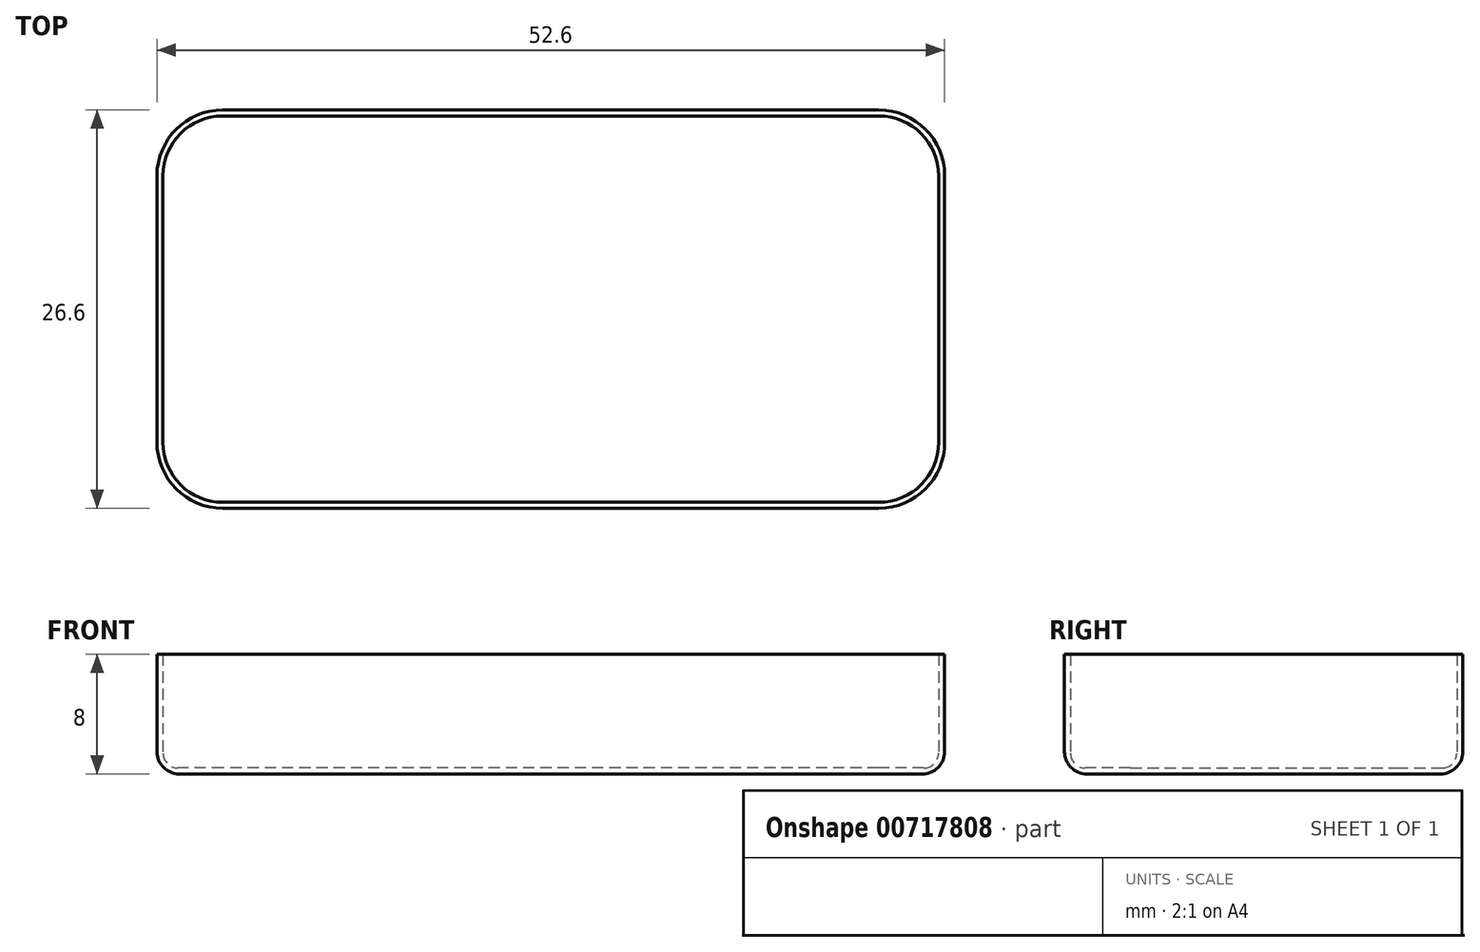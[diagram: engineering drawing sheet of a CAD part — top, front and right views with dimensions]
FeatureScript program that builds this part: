
annotation { "Feature Type Name" : "Feature", "Feature Type Description" : "" }
export const myFeature = defineFeature(function(context is Context, id is Id, definition is map)
    precondition{}
    {
        {
            var Q0;
            Q0=qCreatedBy(makeId("Top.planeOp"),FACE);
            var sketch = newSketch(context, id + "F0", { "sketchPlane" : qUnion([Q0])});
            skLineSegment(sketch, "E0.bottom", {"start": v(26.3, -13.3) * mm, "end": v(-26.3, -13.3) * mm});
            skLineSegment(sketch, "E0.top", {"start": v(26.3, 13.3) * mm, "end": v(-26.3, 13.3) * mm});
            skLineSegment(sketch, "E0.left", {"start": v(26.3, -13.3) * mm, "end": v(26.3, 13.3) * mm});
            skLineSegment(sketch, "E0.right", {"start": v(-26.3, -13.3) * mm, "end": v(-26.3, 13.3) * mm});
            skPoint(sketch, "E0.middle", {"position": v(0, 0) * mm});
            skLineSegment(sketch, "E1.bottom", {"start": v(-25.9, 12.9) * mm, "end": v(25.9, 12.9) * mm});
            skLineSegment(sketch, "E1.top", {"start": v(-25.9, -12.9) * mm, "end": v(25.9, -12.9) * mm});
            skLineSegment(sketch, "E1.left", {"start": v(-25.9, 12.9) * mm, "end": v(-25.9, -12.9) * mm});
            skLineSegment(sketch, "E1.right", {"start": v(25.9, 12.9) * mm, "end": v(25.9, -12.9) * mm});
            skSolve(sketch);
        }
        {
            var Q0;
            Q0=qSketchRegion(id+"F0",true);
            var Q1;
            Q1=makeQuery(id+"F0.imprint","IMPRINT",FACE,{"disambiguationData":[TD([[makeQuery(id+"F0.imprint","IMPRINT",EDGE,{"derivedFrom":sQuery(id+"F0.wireOp",EDGE,"E1.bottom")}),-1.0]])]});
            extrude(context, id + "F1", {"entities" : qUnion([Q0, Q1]), "depth" : .4 * mm, "offsetDistance" : 25 * mm});
        }
        {
            var Q0;
            Q0=makeQuery(id+"F0.imprint","IMPRINT",FACE,{"disambiguationData":[TD([[makeQuery(id+"F0.imprint","IMPRINT",EDGE,{"derivedFrom":sQuery(id+"F0.wireOp",EDGE,"E0.bottom")}),-1.0]])]});
            extrude(context, id + "F2", {"entities" : qUnion([Q0]), "operationType" : NewBodyOperationType.ADD, "depth" : 8 * mm, "offsetDistance" : 25 * mm});
        }
        {
            var Q0;
            Q0=makeQuery(id+"F2.opExtrude","SWEPT_EDGE",EDGE,{"disambiguationData":[OSD([sQuery(id+"F0.wireOp",EDGE,"E1.bottom"),sQuery(id+"F0.wireOp",EDGE,"E1.left")])]});
            var Q1;
            Q1=makeQuery(id+"F2.opExtrude","SWEPT_EDGE",EDGE,{"disambiguationData":[OSD([sQuery(id+"F0.wireOp",EDGE,"E1.bottom"),sQuery(id+"F0.wireOp",EDGE,"E1.right")])]});
            var Q2;
            Q2=makeQuery(id+"F2.opExtrude","SWEPT_EDGE",EDGE,{"disambiguationData":[OSD([sQuery(id+"F0.wireOp",EDGE,"E1.top"),sQuery(id+"F0.wireOp",EDGE,"E1.right")])]});
            var Q3;
            Q3=makeQuery(id+"F2.opExtrude","SWEPT_EDGE",EDGE,{"disambiguationData":[OSD([sQuery(id+"F0.wireOp",EDGE,"E1.top"),sQuery(id+"F0.wireOp",EDGE,"E1.left")])]});
            fillet(context, id + "F3", {"entities" : qUnion([Q0, Q1, Q2, Q3]), "radius" : 4 * mm, "tangentPropagation" : true, "allowEdgeOverflow" : false});
        }
        {
            var Q0;
            {var subQ0=sQuery(id+"F0.wireOp",EDGE,"E0.left");var subQ1=sQuery(id+"F0.wireOp",EDGE,"E0.top");Q0=makeQuery(id+"F2.boolean.opBoolean","MERGE",EDGE,{"derivedFrom":[makeQuery(id+"F1.opExtrude","SWEPT_EDGE",EDGE,{"disambiguationData":[OSD([subQ1,subQ0])]}),makeQuery(id+"F2.opExtrude","SWEPT_EDGE",EDGE,{"disambiguationData":[OSD([subQ1,subQ0])]})]});}
            var Q1;
            {var subQ0=sQuery(id+"F0.wireOp",EDGE,"E0.left");var subQ1=sQuery(id+"F0.wireOp",EDGE,"E0.bottom");Q1=makeQuery(id+"F2.boolean.opBoolean","MERGE",EDGE,{"derivedFrom":[makeQuery(id+"F1.opExtrude","SWEPT_EDGE",EDGE,{"disambiguationData":[OSD([subQ1,subQ0])]}),makeQuery(id+"F2.opExtrude","SWEPT_EDGE",EDGE,{"disambiguationData":[OSD([subQ1,subQ0])]})]});}
            var Q2;
            {var subQ0=sQuery(id+"F0.wireOp",EDGE,"E0.right");var subQ1=sQuery(id+"F0.wireOp",EDGE,"E0.top");Q2=makeQuery(id+"F2.boolean.opBoolean","MERGE",EDGE,{"derivedFrom":[makeQuery(id+"F1.opExtrude","SWEPT_EDGE",EDGE,{"disambiguationData":[OSD([subQ1,subQ0])]}),makeQuery(id+"F2.opExtrude","SWEPT_EDGE",EDGE,{"disambiguationData":[OSD([subQ1,subQ0])]})]});}
            var Q3;
            {var subQ0=sQuery(id+"F0.wireOp",EDGE,"E0.right");var subQ1=sQuery(id+"F0.wireOp",EDGE,"E0.bottom");Q3=makeQuery(id+"F2.boolean.opBoolean","MERGE",EDGE,{"derivedFrom":[makeQuery(id+"F1.opExtrude","SWEPT_EDGE",EDGE,{"disambiguationData":[OSD([subQ1,subQ0])]}),makeQuery(id+"F2.opExtrude","SWEPT_EDGE",EDGE,{"disambiguationData":[OSD([subQ1,subQ0])]})]});}
            fillet(context, id + "F4", {"entities" : qUnion([Q0, Q1, Q2, Q3]), "radius" : 4.4 * mm, "tangentPropagation" : true, "allowEdgeOverflow" : false});
        }
        {
            var Q0;
            Q0=makeQuery(id+"F2.boolean.opBoolean","INTERSECT",EDGE,{"derivedFrom":[makeQuery(id+"F1.opExtrude","CAP_FACE",FACE,{"disambiguationData":[OSD([sQuery(id+"F0.wireOp",EDGE,"E0.bottom"),sQuery(id+"F0.wireOp",EDGE,"E0.top"),sQuery(id+"F0.wireOp",EDGE,"E0.left"),sQuery(id+"F0.wireOp",EDGE,"E0.right")])],"isStart":false}),makeQuery(id+"F2.opExtrude","SWEPT_FACE",FACE,{"disambiguationData":[OSD([sQuery(id+"F0.wireOp",EDGE,"E1.bottom")])]})]});
            fillet(context, id + "F5", {"entities" : qUnion([Q0]), "radius" : 1 * mm, "tangentPropagation" : true, "allowEdgeOverflow" : false});
        }
        {
            var Q0;
            Q0=makeQuery(id+"F1.opExtrude","CAP_EDGE",EDGE,{"disambiguationData":[OSD([sQuery(id+"F0.wireOp",EDGE,"E0.bottom")])],"isStart":true});
            fillet(context, id + "F6", {"entities" : qUnion([Q0]), "radius" : 1.5 * mm, "tangentPropagation" : true, "allowEdgeOverflow" : false});
        }
    });
